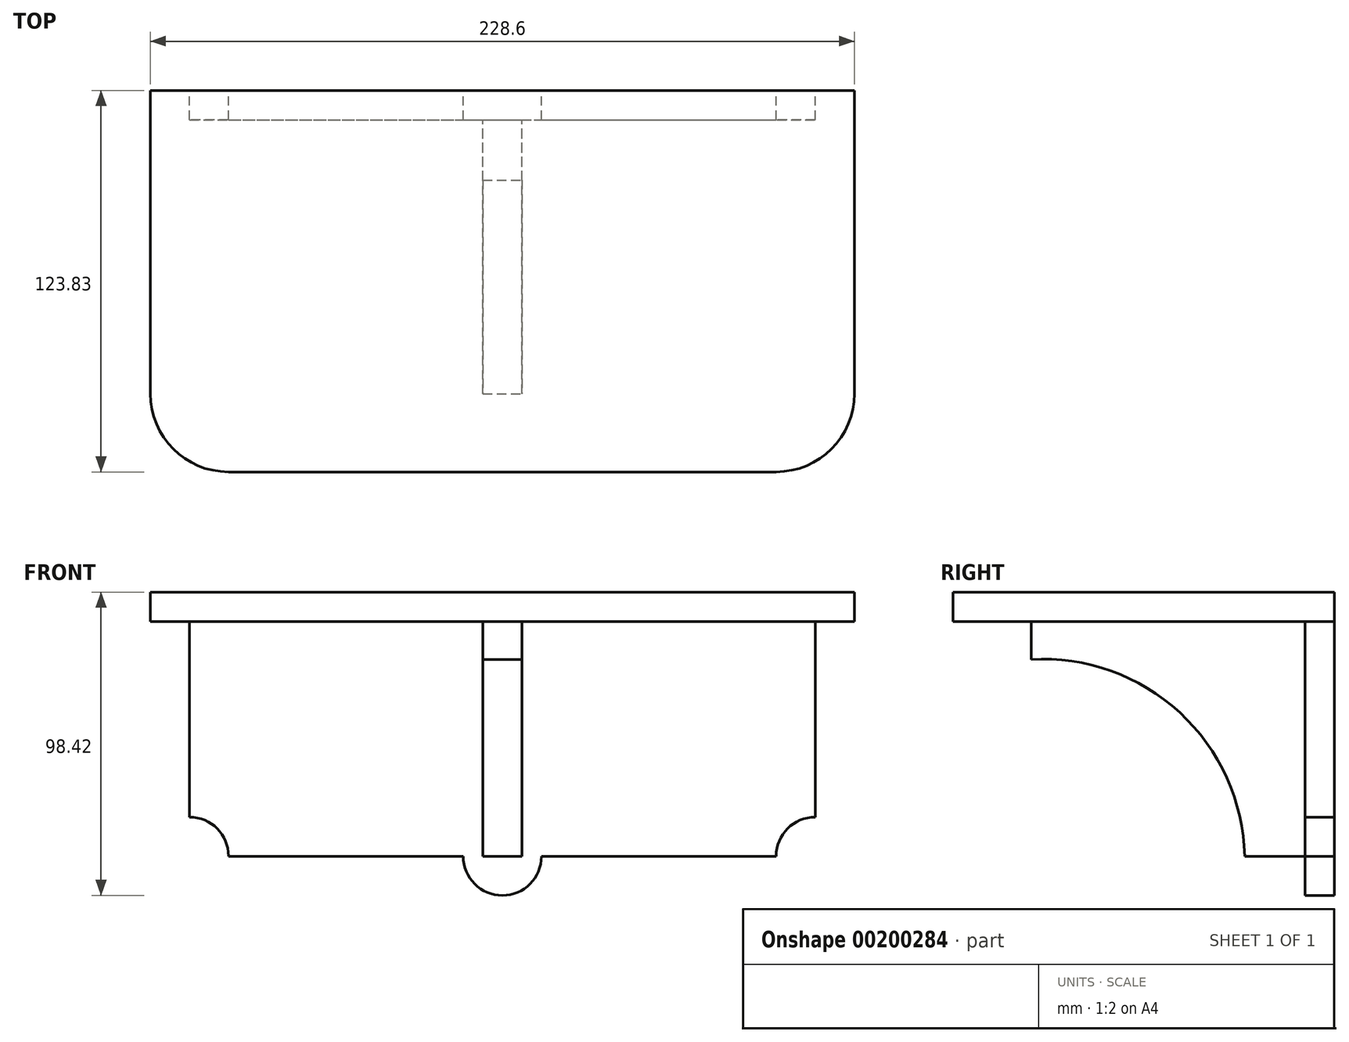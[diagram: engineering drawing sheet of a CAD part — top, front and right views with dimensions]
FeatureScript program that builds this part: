
annotation { "Feature Type Name" : "Feature", "Feature Type Description" : "" }
export const myFeature = defineFeature(function(context is Context, id is Id, definition is map)
    precondition{}
    {
        {
            var Q0;
            Q0=qCreatedBy(makeId("Front.planeOp"),FACE);
            var sketch = newSketch(context, id + "F0", { "sketchPlane" : qUnion([Q0])});
            skLineSegment(sketch, "E0.bottom", {"start": v(-103.01, 17.99) * mm, "end": v(100.19, 17.99) * mm});
            skLineSegment(sketch, "E0.top", {"start": v(-90.31, -58.21) * mm, "end": v(-14.11, -58.21) * mm});
            skLineSegment(sketch, "E0.left", {"start": v(-103.01, 17.99) * mm, "end": v(-103.01, -45.51) * mm});
            skLineSegment(sketch, "E0.right", {"start": v(100.19, 17.99) * mm, "end": v(100.19, -45.51) * mm});
            skArc(sketch, "E1", {"start": v(-14.11, -58.21) * mm, "mid": v(-1.41, -70.91) * mm, "end": v(11.29, -58.21) * mm});
            skLineSegment(sketch, "E2.trimOffspring", {"start": v(11.29, -58.21) * mm, "end": v(87.49, -58.21) * mm});
            skArc(sketch, "E3", {"start": v(-90.31, -58.21) * mm, "mid": v(-94.03, -49.23) * mm, "end": v(-103.01, -45.51) * mm});
            skArc(sketch, "E4", {"start": v(100.19, -45.51) * mm, "mid": v(91.2, -49.23) * mm, "end": v(87.49, -58.21) * mm});
            skSolve(sketch);
        }
        {
            var Q0;
            Q0=makeQuery(id+"F0.imprint","IMPRINT",FACE,{"disambiguationData":[TD([[makeQuery(id+"F0.imprint","IMPRINT",EDGE,{"derivedFrom":sQuery(id+"F0.wireOp",EDGE,"E0.bottom")}),-1.0]])]});
            extrude(context, id + "F1", {"entities" : qUnion([Q0]), "depth" : 9.52 * mm});
        }
        {
            var Q0;
            Q0=makeQuery(id+"F1.opExtrude","SWEPT_FACE",FACE,{"disambiguationData":[OSD([sQuery(id+"F0.wireOp",EDGE,"E0.bottom")])]});
            var sketch = newSketch(context, id + "F2", { "sketchPlane" : qUnion([Q0])});
            skLineSegment(sketch, "E5", {"start": v(-103.01, 0) * mm, "end": v(-115.71, 0) * mm});
            skLineSegment(sketch, "E6", {"start": v(100.19, 0) * mm, "end": v(112.89, 0) * mm});
            skLineSegment(sketch, "E7.bottom", {"start": v(-115.71, 0) * mm, "end": v(112.89, 0) * mm});
            skLineSegment(sketch, "E7.top", {"start": v(-115.71, -9.53) * mm, "end": v(112.89, -9.53) * mm});
            skLineSegment(sketch, "E7.left", {"start": v(-115.71, 0) * mm, "end": v(-115.71, -9.53) * mm});
            skLineSegment(sketch, "E7.right", {"start": v(112.89, 0) * mm, "end": v(112.89, -9.53) * mm});
            skLineSegment(sketch, "E8", {"start": v(-103.01, -9.53) * mm, "end": v(100.19, -9.53) * mm});
            skSolve(sketch);
        }
        {
            var Q0;
            {var subQ2=sQuery(id+"F2.wireOp",EDGE,"E7.right");Q0=makeQuery(id+"F2.imprint","IMPRINT",FACE,{"disambiguationData":[TD([[makeQuery(id+"F2.imprint","IMPRINT",EDGE,{"derivedFrom":subQ2}),-1.0]])]});}
            var Q1;
            {var subQ1=sQuery(id+"F0.wireOp",EDGE,"E0.bottom");var subQ2=makeQuery(id+"F1.opExtrude","SWEPT_EDGE",EDGE,{"disambiguationData":[OSD([subQ1,sQuery(id+"F0.wireOp",EDGE,"E0.left")])]});Q1=makeQuery(id+"F2.imprint","IMPRINT",FACE,{"disambiguationData":[TD([[makeQuery(id+"F2.imprint","IMPRINT",EDGE,{"derivedFrom":subQ2}),-1.0]])]});}
            var Q2;
            {var subQ2=sQuery(id+"F2.wireOp",EDGE,"E7.left");Q2=makeQuery(id+"F2.imprint","IMPRINT",FACE,{"disambiguationData":[TD([[makeQuery(id+"F2.imprint","IMPRINT",EDGE,{"derivedFrom":subQ2}),1.0]])]});}
            extrude(context, id + "F3", {"entities" : qUnion([Q0, Q1, Q2]), "operationType" : NewBodyOperationType.ADD, "depth" : 9.52 * mm});
        }
        {
            var Q0;
            Q0=makeQuery(id+"F3.boolean.opBoolean","MERGE",FACE,{"derivedFrom":[makeQuery(id+"F1.opExtrude","CAP_FACE",FACE,{"disambiguationData":[OSD([sQuery(id+"F0.wireOp",EDGE,"E0.bottom"),sQuery(id+"F0.wireOp",EDGE,"E0.left"),sQuery(id+"F0.wireOp",EDGE,"E0.right"),sQuery(id+"F0.wireOp",EDGE,"E0.top"),sQuery(id+"F0.wireOp",EDGE,"E1"),sQuery(id+"F0.wireOp",EDGE,"E2.trimOffspring"),sQuery(id+"F0.wireOp",EDGE,"E3"),sQuery(id+"F0.wireOp",EDGE,"E4")])],"isStart":false}),makeQuery(id+"F3.opExtrude","SWEPT_FACE",FACE,{"disambiguationData":[OSD([sQuery(id+"F2.wireOp",EDGE,"E7.top"),sQuery(id+"F2.wireOp",EDGE,"E8")])]})]});
            var sketch = newSketch(context, id + "F4", { "sketchPlane" : qUnion([Q0])});
            skLineSegment(sketch, "E9", {"start": v(-103.01, 17.99) * mm, "end": v(100.19, 17.99) * mm});
            skSolve(sketch);
        }
        {
            var Q0;
            Q0=makeQuery(id+"F4.imprint","IMPRINT",FACE,{"disambiguationData":[TD([[makeQuery(id+"F4.imprint","IMPRINT",EDGE,{"derivedFrom":sQuery(id+"F4.wireOp",EDGE,"E9")}),1.0]])]});
            extrude(context, id + "F5", {"entities" : qUnion([Q0]), "operationType" : NewBodyOperationType.ADD, "depth" : 114.3 * mm});
        }
        {
            var Q0;
            {var subQ0=sQuery(id+"F2.wireOp",EDGE,"E8");var subQ1=sQuery(id+"F2.wireOp",EDGE,"E7.top");Q0=makeQuery(id+"F5.boolean.opBoolean","MERGE",FACE,{"derivedFrom":[makeQuery(id+"F3.opExtrude","CAP_FACE",FACE,{"disambiguationData":[OSD([sQuery(id+"F2.wireOp",EDGE,"E7.bottom"),subQ1,sQuery(id+"F2.wireOp",EDGE,"E7.left"),sQuery(id+"F2.wireOp",EDGE,"E7.right"),subQ0])],"isStart":false}),makeQuery(id+"F5.opExtrude","SWEPT_FACE",FACE,{"disambiguationData":[OSD([subQ1,subQ0])]})]});}
            var sketch = newSketch(context, id + "F6", { "sketchPlane" : qUnion([Q0])});
            skLineSegment(sketch, "E10", {"start": v(-115.71, 0) * mm, "end": v(-115.71, -98.43) * mm});
            skLineSegment(sketch, "E11", {"start": v(-90.31, -123.83) * mm, "end": v(87.49, -123.83) * mm});
            skLineSegment(sketch, "E12", {"start": v(112.89, -98.43) * mm, "end": v(112.89, 0) * mm});
            skLineSegment(sketch, "E13", {"start": v(112.89, 0) * mm, "end": v(-115.71, 0) * mm});
            skPoint(sketch, "E14.visualSharp", {"position": v(-115.71, -123.83) * mm});
            skArc(sketch, "E14.filletArc", {"start": v(-115.71, -98.43) * mm, "mid": v(-108.27, -116.39) * mm, "end": v(-90.31, -123.83) * mm});
            skPoint(sketch, "E15.visualSharp", {"position": v(112.89, -123.83) * mm});
            skArc(sketch, "E15.filletArc", {"start": v(87.49, -123.83) * mm, "mid": v(105.45, -116.39) * mm, "end": v(112.89, -98.43) * mm});
            skSolve(sketch);
        }
        {
            var Q0;
            {var subQ0=sQuery(id+"F6.wireOp",EDGE,"E14.filletArc");Q0=makeQuery(id+"F6.imprint","IMPRINT",FACE,{"disambiguationData":[TD([[makeQuery(id+"F6.imprint","IMPRINT",EDGE,{"derivedFrom":subQ0}),-1.0]])]});}
            extrude(context, id + "F7", {"entities" : qUnion([Q0]), "operationType" : NewBodyOperationType.REMOVE, "oppositeDirection" : true, "depth" : 9.65 * mm});
        }
        {
            var Q0;
            {var subQ0=sQuery(id+"F6.wireOp",EDGE,"E15.filletArc");Q0=makeQuery(id+"F6.imprint","IMPRINT",FACE,{"disambiguationData":[TD([[makeQuery(id+"F6.imprint","IMPRINT",EDGE,{"derivedFrom":subQ0}),-1.0]])]});}
            extrude(context, id + "F8", {"entities" : qUnion([Q0]), "operationType" : NewBodyOperationType.REMOVE, "oppositeDirection" : true, "depth" : 25.4 * mm});
        }
        {
            var Q0;
            Q0=makeQuery(id+"F3.boolean.opBoolean","MERGE",FACE,{"derivedFrom":[makeQuery(id+"F1.opExtrude","CAP_FACE",FACE,{"disambiguationData":[OSD([sQuery(id+"F0.wireOp",EDGE,"E0.bottom"),sQuery(id+"F0.wireOp",EDGE,"E0.left"),sQuery(id+"F0.wireOp",EDGE,"E0.right"),sQuery(id+"F0.wireOp",EDGE,"E0.top"),sQuery(id+"F0.wireOp",EDGE,"E1"),sQuery(id+"F0.wireOp",EDGE,"E2.trimOffspring"),sQuery(id+"F0.wireOp",EDGE,"E3"),sQuery(id+"F0.wireOp",EDGE,"E4")])],"isStart":false}),makeQuery(id+"F3.opExtrude","SWEPT_FACE",FACE,{"disambiguationData":[OSD([sQuery(id+"F2.wireOp",EDGE,"E7.top"),sQuery(id+"F2.wireOp",EDGE,"E8")])]})]});
            var sketch = newSketch(context, id + "F9", { "sketchPlane" : qUnion([Q0])});
            skLineSegment(sketch, "E16.bottom", {"start": v(-7.76, 17.99) * mm, "end": v(4.94, 17.99) * mm});
            skLineSegment(sketch, "E16.top", {"start": v(-7.76, -58.21) * mm, "end": v(4.94, -58.21) * mm});
            skLineSegment(sketch, "E16.left", {"start": v(-7.76, 17.99) * mm, "end": v(-7.76, -58.21) * mm});
            skLineSegment(sketch, "E16.right", {"start": v(4.94, 17.99) * mm, "end": v(4.94, -58.21) * mm});
            skSolve(sketch);
        }
        {
            var Q0;
            Q0=makeQuery(id+"F9.imprint","IMPRINT",FACE,{"disambiguationData":[TD([[makeQuery(id+"F9.imprint","IMPRINT",EDGE,{"derivedFrom":sQuery(id+"F9.wireOp",EDGE,"E16.bottom")}),-1.0]])]});
            extrude(context, id + "F10", {"entities" : qUnion([Q0]), "operationType" : NewBodyOperationType.ADD, "depth" : 88.9 * mm});
        }
        {
            var Q0;
            Q0=makeQuery(id+"F10.opExtrude","SWEPT_FACE",FACE,{"disambiguationData":[OSD([sQuery(id+"F9.wireOp",EDGE,"E16.right")])]});
            var sketch = newSketch(context, id + "F11", { "sketchPlane" : qUnion([Q0])});
            skLineSegment(sketch, "E17", {"start": v(-98.43, 17.99) * mm, "end": v(-98.43, 5.29) * mm});
            skLineSegment(sketch, "E18", {"start": v(-9.53, -58.21) * mm, "end": v(-28.58, -58.21) * mm});
            skLineSegment(sketch, "E19", {"start": v(-98.43, -58.21) * mm, "end": v(-9.52, -58.21) * mm});
            skLineSegment(sketch, "E20", {"start": v(-98.43, 17.99) * mm, "end": v(-98.43, -58.21) * mm});
            skArc(sketch, "E21", {"start": v(-29.13, -58.21) * mm, "mid": v(-50.22, -11.57) * mm, "end": v(-98.42, 5.66) * mm});
            skSolve(sketch);
        }
        {
            var Q0;
            {var subQ3=sQuery(id+"F11.wireOp",EDGE,"E21");Q0=makeQuery(id+"F11.imprint","IMPRINT",FACE,{"disambiguationData":[TD([[makeQuery(id+"F11.imprint","IMPRINT",EDGE,{"derivedFrom":subQ3}),1.0]])]});}
            extrude(context, id + "F12", {"entities" : qUnion([Q0]), "operationType" : NewBodyOperationType.REMOVE, "oppositeDirection" : true, "depth" : 25.4 * mm});
        }
    });
